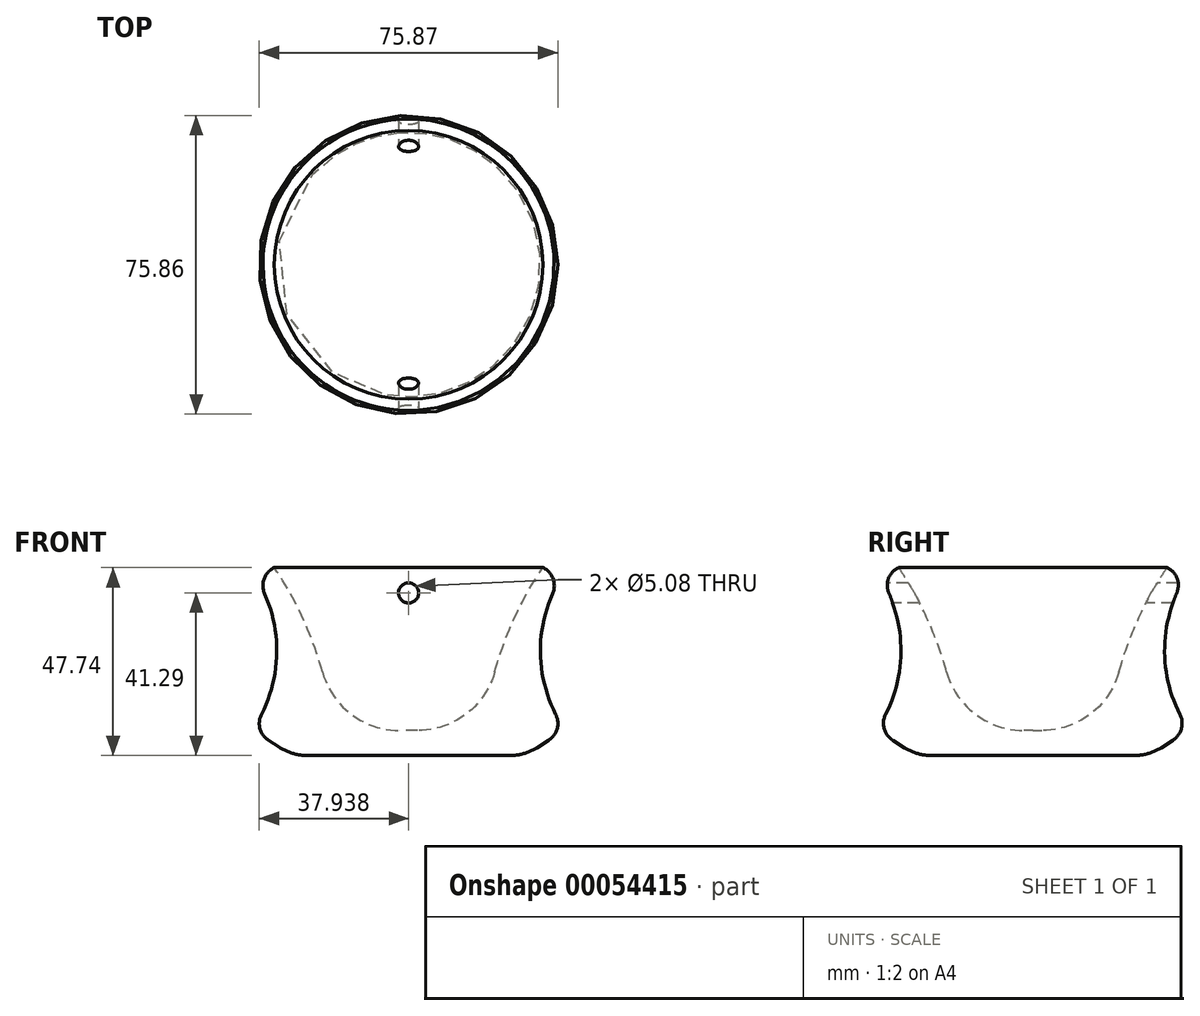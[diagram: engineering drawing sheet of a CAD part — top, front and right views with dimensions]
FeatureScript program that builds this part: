
annotation { "Feature Type Name" : "Feature", "Feature Type Description" : "" }
export const myFeature = defineFeature(function(context is Context, id is Id, definition is map)
    precondition{}
    {
        {
            var Q0;
            Q0=qCreatedBy(makeId("Front.planeOp"),FACE);
            var sketch = newSketch(context, id + "F0", { "sketchPlane" : qUnion([Q0])});
            skLineSegment(sketch, "E0", {"start": v(-5.27, -41.29) * mm, "end": v(13.78, -41.29) * mm});
            skLineSegment(sketch, "E1", {"start": v(-22.65, 6.45) * mm, "end": v(-16.3, 6.45) * mm});
            skLineSegment(sketch, "E2", {"start": v(-1.23, -34.94) * mm, "end": v(17.82, -34.94) * mm});
            skLineSegment(sketch, "E3", {"start": v(13.78, -41.29) * mm, "end": v(17.82, -41.29) * mm});
            skLineSegment(sketch, "E4", {"start": v(17.82, -34.94) * mm, "end": v(17.82, -41.29) * mm});
            skLineSegment(sketch, "E5", {"start": v(17.82, -26.78) * mm, "end": v(17.82, -10.52) * mm});
            skLineSegment(sketch, "E6", {"start": v(-5.27, -41.29) * mm, "end": v(-11.7, -41.29) * mm});
            skArc(sketch, "E7", {"start": v(-1.23, -34.94) * mm, "mid": v(-6.23, -13.33) * mm, "end": v(-16.3, 6.45) * mm});
            skPoint(sketch, "E8.start.orphan", {"position": v(-7.58, -34.94) * mm});
            skLineSegment(sketch, "E9", {"start": v(-11.7, -41.29) * mm, "end": v(-21.92, -34.8) * mm});
            skArc(sketch, "E10", {"start": v(-21.92, -34.8) * mm, "mid": v(-15.67, -14.06) * mm, "end": v(-22.65, 6.45) * mm});
            skSolve(sketch);
        }
        {
            var Q0;
            Q0=qCreatedBy(makeId("Front.planeOp"),FACE);
            var sketch = newSketch(context, id + "F1", { "sketchPlane" : qUnion([Q0])});
            skLineSegment(sketch, "E11", {"start": v(0, 0) * mm, "end": v(17.82, 0) * mm});
            skCircle(sketch, "E12", {"center": v(17.82, 0) * mm, "radius": 2.54 * mm});
            skSolve(sketch);
        }
        {
            var Q0;
            Q0 = qSketchRegion(id + "F0", true);
            var Q1;
            Q1=sQuery(id+"F0.wireOp",EDGE,"E5");
            revolve(context, id + "F2", {"entities" : qUnion([Q0]), "axis" : qUnion([Q1]), "revolveType" : RevolveType.FULL});
        }
        {
            var Q0;
            Q0=makeQuery(id+"F1.imprint","IMPRINT",FACE,{"disambiguationData":[TD([[makeQuery(id+"F1.imprint","IMPRINT",EDGE,{"derivedFrom":sQuery(id+"F1.wireOp",EDGE,"E12")}),1.0]])]});
            extrude(context, id + "F3", {"entities" : qUnion([Q0]), "operationType" : NewBodyOperationType.REMOVE, "oppositeDirection" : true, "depth" : 127 * mm, "hasSecondDirection" : true, "secondDirectionOppositeDirection" : false, "secondDirectionDepth" : 127 * mm});
        }
        {
            var Q0;
            Q0=makeQuery(id+"F2.opRevolve","SWEPT_EDGE",EDGE,{"disambiguationData":[OSD([sQuery(id+"F0.wireOp",EDGE,"E2"),sQuery(id+"F0.wireOp",EDGE,"E7")])]});
            fillet(context, id + "F4", {"entities" : qUnion([Q0]), "radius" : 20.32 * mm, "tangentPropagation" : true, "allowEdgeOverflow" : false});
        }
        {
            var Q0;
            Q0=makeQuery(id+"F2.opRevolve","SWEPT_EDGE",EDGE,{"disambiguationData":[OSD([sQuery(id+"F0.wireOp",EDGE,"E1"),sQuery(id+"F0.wireOp",EDGE,"E10")])]});
            fillet(context, id + "F5", {"entities" : qUnion([Q0]), "radius" : 5.08 * mm, "tangentPropagation" : true, "allowEdgeOverflow" : false});
        }
        {
            var Q0;
            Q0=makeQuery(id+"F2.opRevolve","SWEPT_EDGE",EDGE,{"disambiguationData":[OSD([sQuery(id+"F0.wireOp",EDGE,"E9"),sQuery(id+"F0.wireOp",EDGE,"E10")])]});
            fillet(context, id + "F6", {"entities" : qUnion([Q0]), "radius" : 5.08 * mm, "tangentPropagation" : true, "allowEdgeOverflow" : false});
        }
        {
            var Q0;
            Q0=makeQuery(id+"F2.opRevolve","SWEPT_EDGE",EDGE,{"disambiguationData":[OSD([sQuery(id+"F0.wireOp",EDGE,"E6"),sQuery(id+"F0.wireOp",EDGE,"E9")])]});
            fillet(context, id + "F7", {"entities" : qUnion([Q0]), "radius" : 12.7 * mm, "tangentPropagation" : true, "allowEdgeOverflow" : false});
        }
    });
